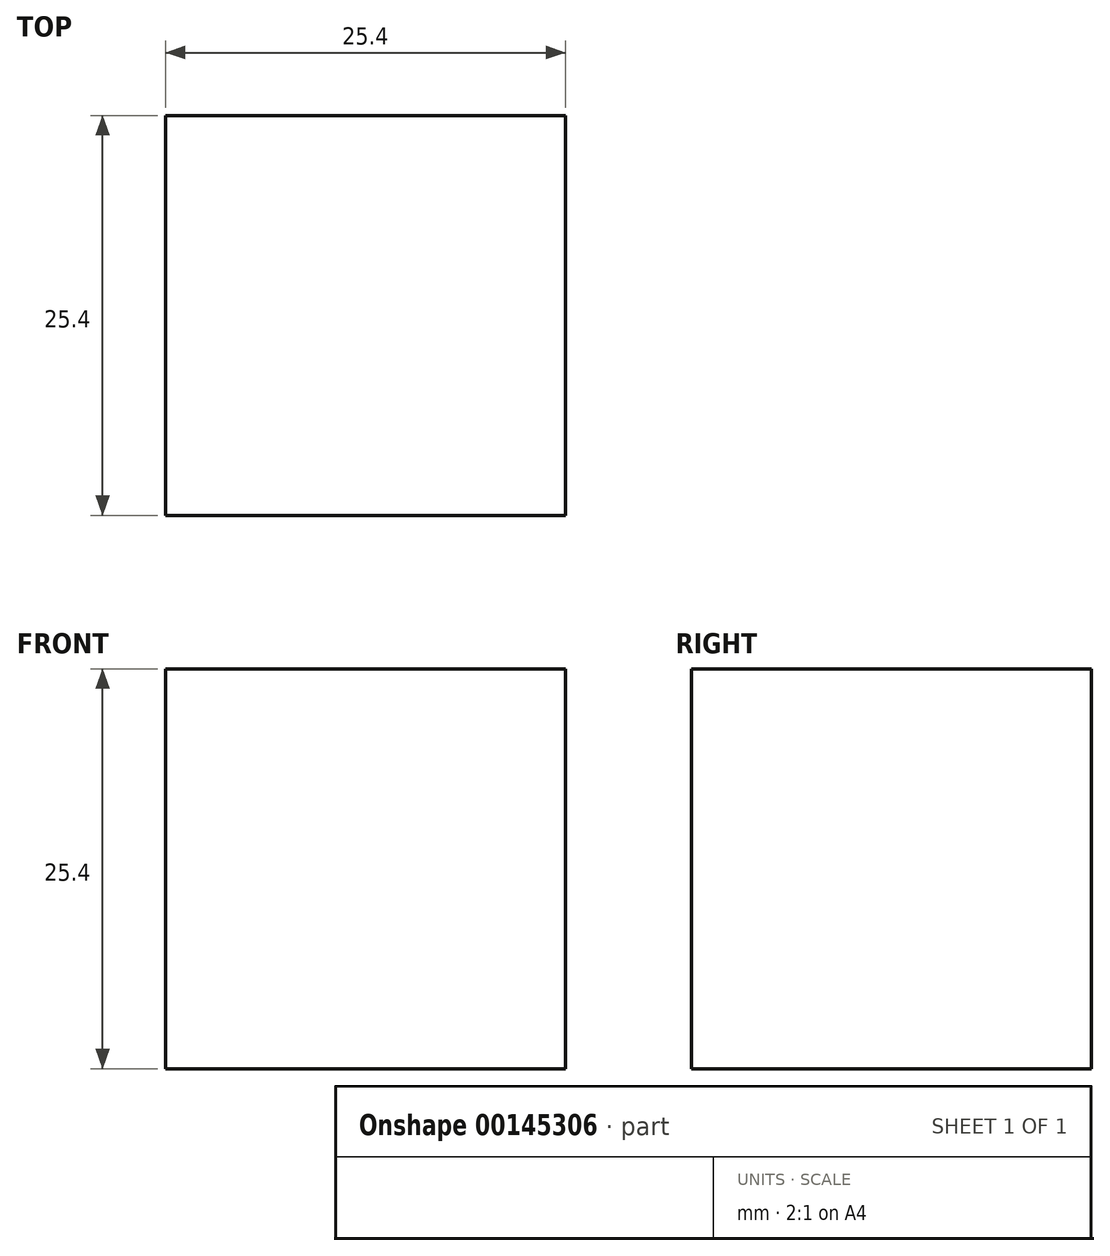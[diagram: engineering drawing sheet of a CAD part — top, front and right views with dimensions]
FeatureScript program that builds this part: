
annotation { "Feature Type Name" : "Feature", "Feature Type Description" : "" }
export const myFeature = defineFeature(function(context is Context, id is Id, definition is map)
    precondition{}
    {
        {
            var Q0;
            Q0=qCreatedBy(makeId("Front.planeOp"),FACE);
            var sketch = newSketch(context, id + "F0", { "sketchPlane" : qUnion([Q0])});
            skLineSegment(sketch, "E0", {"start": v(0, 0) * mm, "end": v(0, 25.4) * mm});
            skLineSegment(sketch, "E1", {"start": v(0, 25.4) * mm, "end": v(25.4, 25.4) * mm});
            skLineSegment(sketch, "E2", {"start": v(25.4, 25.4) * mm, "end": v(25.4, 0) * mm});
            skLineSegment(sketch, "E3", {"start": v(25.4, 0) * mm, "end": v(0, 0) * mm});
            skSolve(sketch);
        }
        {
            var Q0;
            Q0=makeQuery(id+"F0.imprint","IMPRINT",FACE,{"disambiguationData":[TD([[makeQuery(id+"F0.imprint","IMPRINT",EDGE,{"derivedFrom":sQuery(id+"F0.wireOp",EDGE,"E0")}),-1.0]])]});
            extrude(context, id + "F1", {"entities" : qUnion([Q0]), "depth" : 25.4 * mm});
        }
    });
